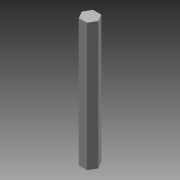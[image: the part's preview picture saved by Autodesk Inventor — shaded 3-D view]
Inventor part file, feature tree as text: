
AUTODESK INVENTOR PART (.ipt)
format: ipt  version: 2014 (Build 180170000, 170)  size: 75,264 bytes
history: native  units: in
note: dims shown in document units (in); Inventor stores cm internally (conversion verified against a paired STEP export)
features: extrude x1, sketch x1
ambient origin geometry x8: Origin, YZ Plane, XZ Plane, XY Plane, X Axis, Y Axis, Z Axis, Center Point
bodies: Solid1 (feature_tree)
feature tree (2):
  extrude  "Extrusion1"  Depth=4.5in TaperAngle=0.0deg
  sketch  "Sketch1"  dims[d0=0.5in d1=4.5in d2=0.0in]
